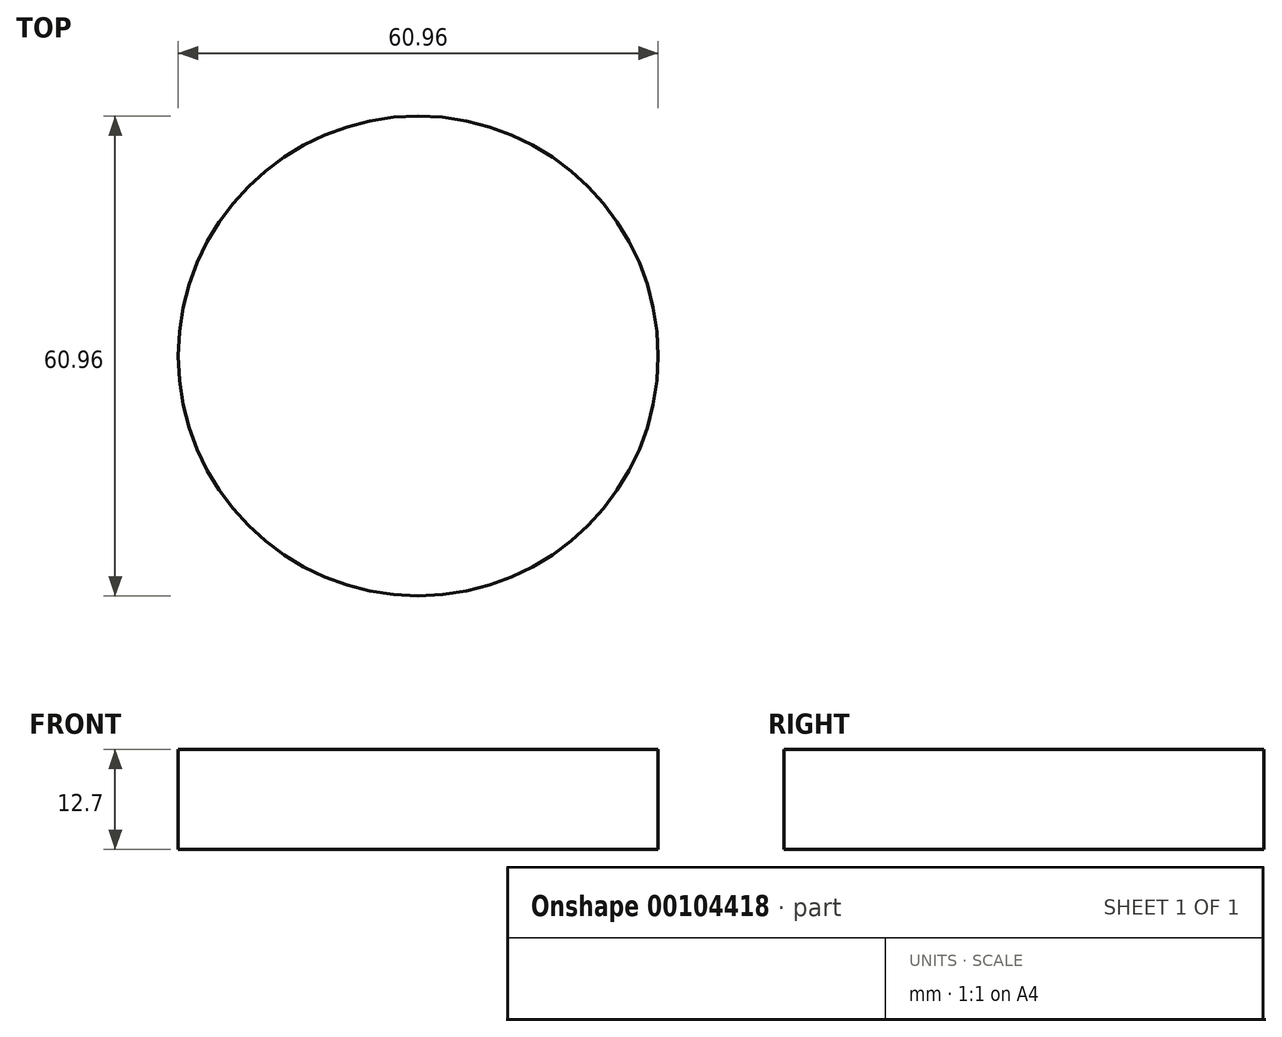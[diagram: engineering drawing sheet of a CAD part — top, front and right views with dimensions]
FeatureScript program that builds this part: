
annotation { "Feature Type Name" : "Feature", "Feature Type Description" : "" }
export const myFeature = defineFeature(function(context is Context, id is Id, definition is map)
    precondition{}
    {
        {
            var Q0;
            Q0=qCreatedBy(makeId("Top.planeOp"),FACE);
            var sketch = newSketch(context, id + "F0", { "sketchPlane" : qUnion([Q0])});
            skCircle(sketch, "E0", {"center": v(0, 0) * mm, "radius": 30.48 * mm});
            skSolve(sketch);
        }
        {
            var Q0;
            Q0=makeQuery(id+"F0.imprint","IMPRINT",FACE,{"disambiguationData":[TD([[makeQuery(id+"F0.imprint","IMPRINT",EDGE,{"derivedFrom":sQuery(id+"F0.wireOp",EDGE,"E0")}),1.0]])]});
            extrude(context, id + "F1", {"entities" : qUnion([Q0]), "depth" : 12.7 * mm});
        }
        {
            var Q0;
            Q0=makeQuery(id+"F1.opExtrude","CAP_FACE",FACE,{"disambiguationData":[OSD([sQuery(id+"F0.wireOp",EDGE,"E0")])],"isStart":false});
            var sketch = newSketch(context, id + "F2", { "sketchPlane" : qUnion([Q0])});
            skCircle(sketch, "E1.cCircle", {"center": v(0, 0) * mm, "radius": 30.48 * mm, "construction": true});
            skLineSegment(sketch, "E1.0", {"start": v(-12.63, 30.48) * mm, "end": v(12.63, 30.48) * mm});
            skLineSegment(sketch, "E1.1", {"start": v(12.63, 30.48) * mm, "end": v(30.48, 12.63) * mm});
            skLineSegment(sketch, "E1.2", {"start": v(30.48, 12.63) * mm, "end": v(30.48, -12.63) * mm});
            skLineSegment(sketch, "E1.3", {"start": v(30.48, -12.63) * mm, "end": v(12.63, -30.48) * mm});
            skLineSegment(sketch, "E1.4", {"start": v(12.63, -30.48) * mm, "end": v(-12.63, -30.48) * mm});
            skLineSegment(sketch, "E1.5", {"start": v(-12.63, -30.48) * mm, "end": v(-30.48, -12.63) * mm});
            skLineSegment(sketch, "E1.6", {"start": v(-30.48, -12.63) * mm, "end": v(-30.48, 12.63) * mm});
            skLineSegment(sketch, "E1.7", {"start": v(-30.48, 12.63) * mm, "end": v(-12.63, 30.48) * mm});
            skPoint(sketch, "E1.0.midPoint", {"position": v(0, 30.48) * mm});
            skSolve(sketch);
        }
        {
            var Q0;
            {var subQ0=makeQuery(id+"F1.opExtrude","CAP_EDGE",EDGE,{"disambiguationData":[OSD([sQuery(id+"F0.wireOp",EDGE,"E0")])],"isStart":false});var subQ5=makeQuery(id+"F2.imprint","INTERSECT",VERTEX,{"derivedFrom":[subQ0,sQuery(id+"F2.wireOp",EDGE,"E1.0")]});Q0=makeQuery(id+"F2.imprint","IMPRINT",FACE,{"disambiguationData":[TD([[makeQuery(id+"F2.imprint","IMPRINT",EDGE,{"disambiguationData":[TD([[subQ5,1.0]])],"derivedFrom":subQ0}),1.0]])]});}
            cPlane(context, id + "F3", {"entities" : qUnion([Q0]), "cplaneType" : CPlaneType.OFFSET, "offset" : 76.2 * mm, "width" : 152.4 * mm, "height" : 152.4 * mm});
        }
    });
